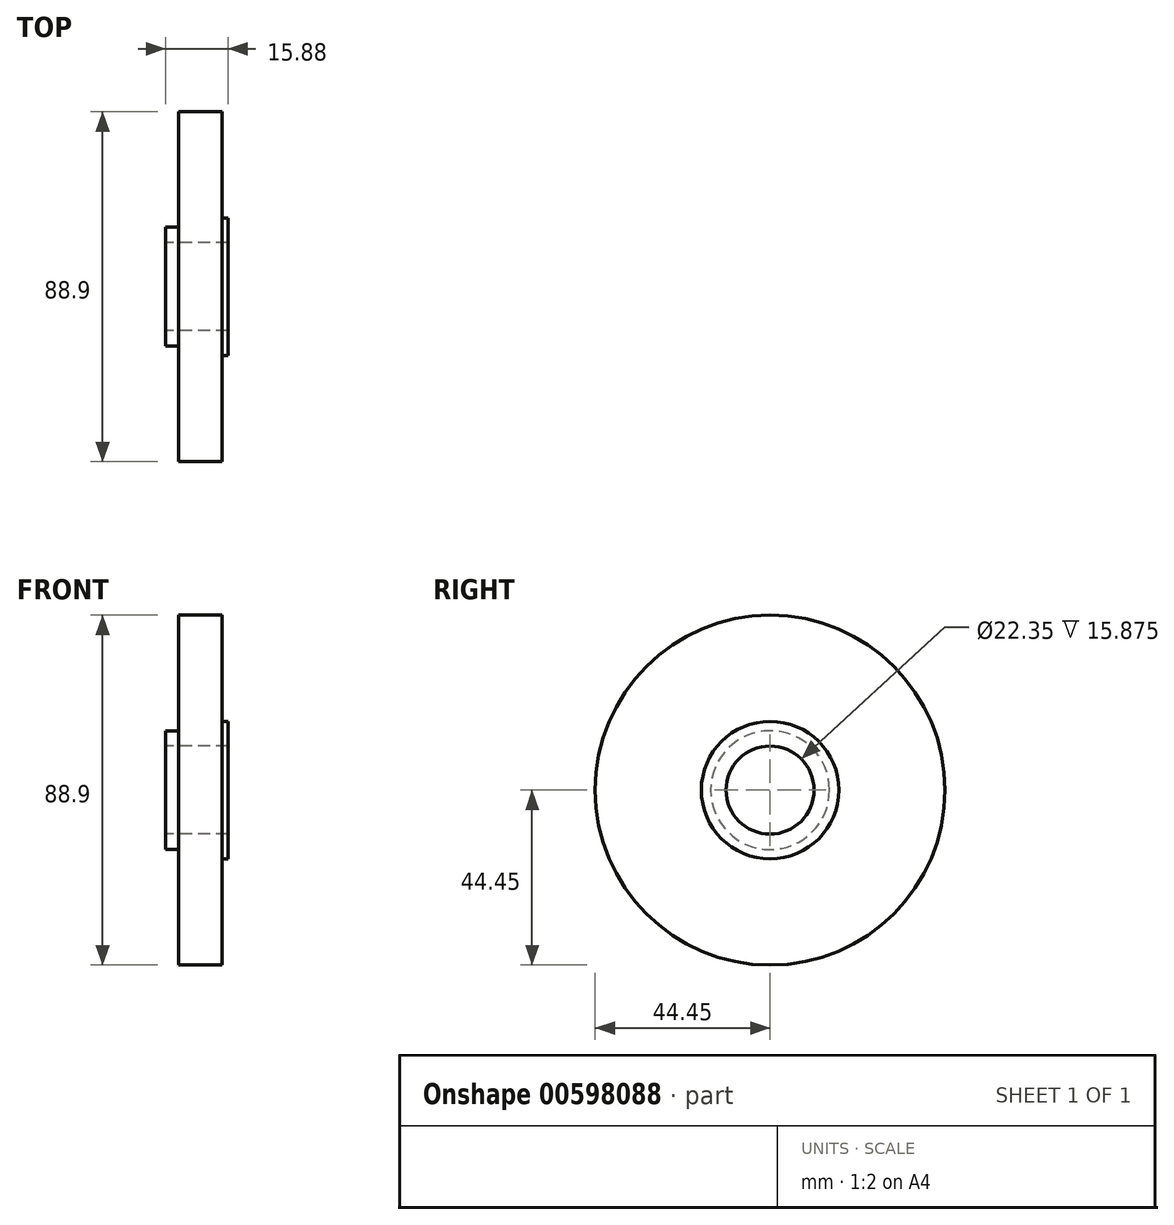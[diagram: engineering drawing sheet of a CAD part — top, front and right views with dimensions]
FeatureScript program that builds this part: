
annotation { "Feature Type Name" : "Feature", "Feature Type Description" : "" }
export const myFeature = defineFeature(function(context is Context, id is Id, definition is map)
    precondition{}
    {
        {
            var Q0;
            Q0=qCreatedBy(makeId("Front.planeOp"),FACE);
            var sketch = newSketch(context, id + "F0", { "sketchPlane" : qUnion([Q0])});
            skLineSegment(sketch, "E0", {"start": v(0, 11.18) * mm, "end": v(15.88, 11.18) * mm});
            skLineSegment(sketch, "E1", {"start": v(15.88, 11.18) * mm, "end": v(15.88, 17.46) * mm});
            skLineSegment(sketch, "E2", {"start": v(15.88, 17.46) * mm, "end": v(14.35, 17.46) * mm});
            skLineSegment(sketch, "E3", {"start": v(14.35, 17.46) * mm, "end": v(14.35, 44.45) * mm});
            skLineSegment(sketch, "E4", {"start": v(14.35, 44.45) * mm, "end": v(3.25, 44.45) * mm});
            skLineSegment(sketch, "E5", {"start": v(3.25, 44.45) * mm, "end": v(3.25, 15.09) * mm});
            skLineSegment(sketch, "E6", {"start": v(3.25, 15.09) * mm, "end": v(0, 15.09) * mm});
            skLineSegment(sketch, "E7", {"start": v(0, 15.09) * mm, "end": v(0, 11.18) * mm});
            skLineSegment(sketch, "E8", {"start": v(-75.6, 0) * mm, "end": v(75.43, 0) * mm, "construction": true});
            skSolve(sketch);
        }
        {
            var Q0;
            Q0 = qSketchRegion(id + "F0", true);
            var Q1;
            Q1=sQuery(id+"F0.wireOp",EDGE,"E8");
            revolve(context, id + "F1", {"entities" : qUnion([Q0]), "axis" : qUnion([Q1]), "revolveType" : RevolveType.FULL});
        }
    });
